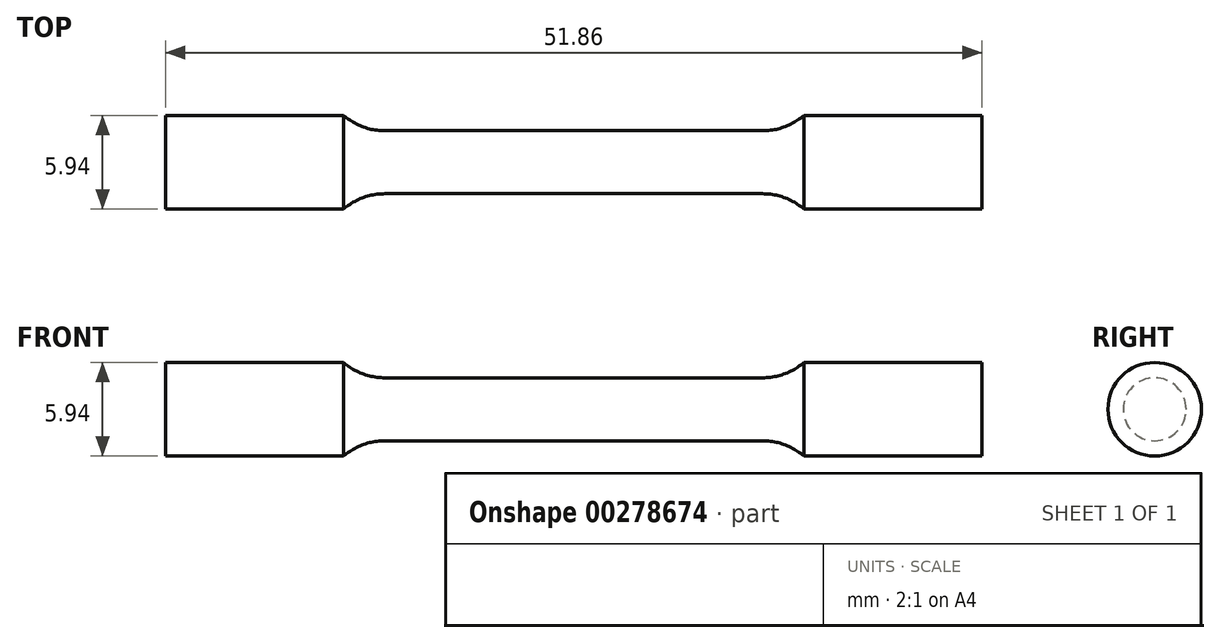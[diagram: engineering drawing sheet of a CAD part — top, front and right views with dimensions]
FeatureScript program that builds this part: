
annotation { "Feature Type Name" : "Feature", "Feature Type Description" : "" }
export const myFeature = defineFeature(function(context is Context, id is Id, definition is map)
    precondition{}
    {
        {
            var Q0;
            Q0=qCreatedBy(makeId("Front.planeOp"),FACE);
            var sketch = newSketch(context, id + "F0", { "sketchPlane" : qUnion([Q0])});
            skLineSegment(sketch, "E0", {"start": v(0, 2) * mm, "end": v(12, 2) * mm});
            skArc(sketch, "E1", {"start": v(12, 2) * mm, "mid": v(13.4, 2.25) * mm, "end": v(14.61, 2.97) * mm});
            skLineSegment(sketch, "E2", {"start": v(14.61, 2.97) * mm, "end": v(25.93, 2.97) * mm});
            skLineSegment(sketch, "E3", {"start": v(25.93, 2.97) * mm, "end": v(25.93, 0) * mm});
            skLineSegment(sketch, "E4.MirrorCS", {"start": v(0, 2) * mm, "end": v(-12, 2) * mm});
            skLineSegment(sketch, "E5.MirrorCS", {"start": v(-25.93, 2.97) * mm, "end": v(-25.93, 0) * mm});
            skLineSegment(sketch, "E6.MirrorCS", {"start": v(-14.61, 2.97) * mm, "end": v(-25.93, 2.97) * mm});
            skArc(sketch, "E7.MirrorCS", {"start": v(-12, 2) * mm, "mid": v(-13.4, 2.25) * mm, "end": v(-14.61, 2.97) * mm});
            skLineSegment(sketch, "E8", {"start": v(-25.93, 0) * mm, "end": v(25.93, 0) * mm});
            skSolve(sketch);
        }
        {
            var Q0;
            Q0 = qSketchRegion(id + "F0", true);
            var Q1;
            Q1=sQuery(id+"F0.wireOp",EDGE,"E8");
            revolve(context, id + "F1", {"entities" : qUnion([Q0]), "axis" : qUnion([Q1]), "revolveType" : RevolveType.FULL});
        }
    });
